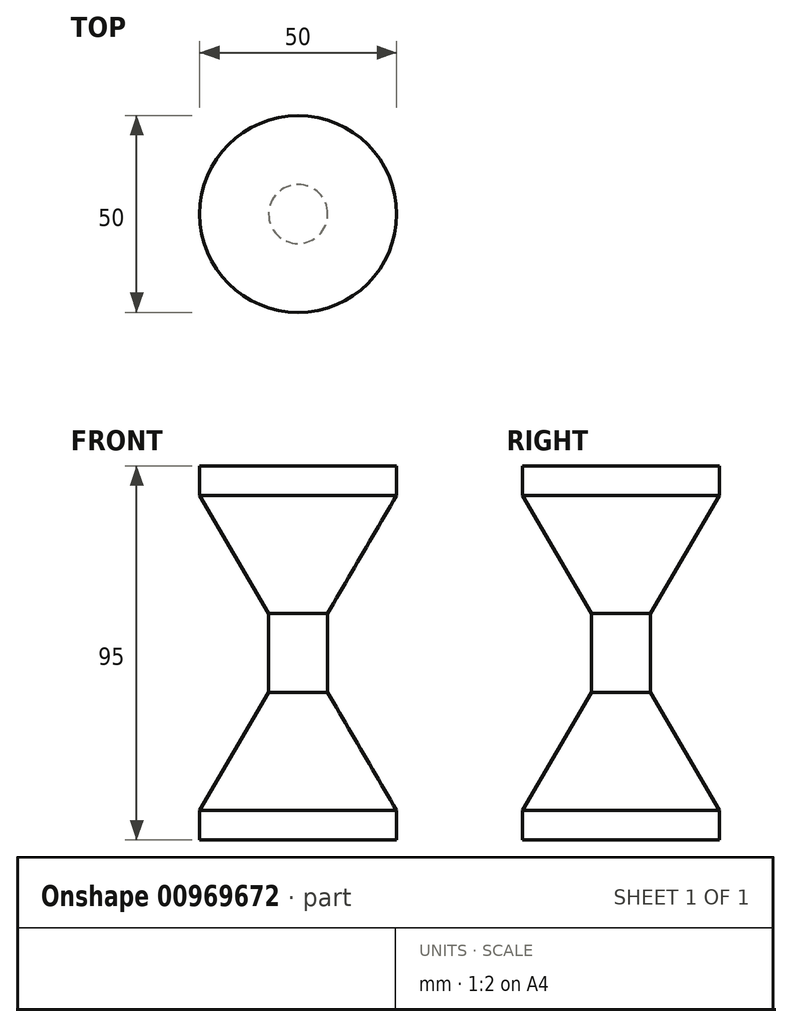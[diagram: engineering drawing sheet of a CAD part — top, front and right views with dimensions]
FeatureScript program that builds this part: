
annotation { "Feature Type Name" : "Feature", "Feature Type Description" : "" }
export const myFeature = defineFeature(function(context is Context, id is Id, definition is map)
    precondition{}
    {
        {
            var Q0;
            Q0=qCreatedBy(makeId("Right.planeOp"),FACE);
            var sketch = newSketch(context, id + "F0", { "sketchPlane" : qUnion([Q0])});
            skLineSegment(sketch, "E0", {"start": v(7.5, 10) * mm, "end": v(7.5, 0) * mm});
            skLineSegment(sketch, "E1", {"start": v(7.5, 10) * mm, "end": v(25, 40) * mm});
            skLineSegment(sketch, "E2", {"start": v(25, 40) * mm, "end": v(25, 47.5) * mm});
            skLineSegment(sketch, "E3.MirrorCS", {"start": v(7.5, -10) * mm, "end": v(7.5, 0) * mm});
            skLineSegment(sketch, "E4.MirrorCS", {"start": v(7.5, -10) * mm, "end": v(25, -40) * mm});
            skLineSegment(sketch, "E5.MirrorCS", {"start": v(25, -40) * mm, "end": v(25, -47.5) * mm});
            skLineSegment(sketch, "E6", {"start": v(0, 47.5) * mm, "end": v(0, -47.5) * mm, "construction": true});
            skLineSegment(sketch, "E7", {"start": v(25, 47.5) * mm, "end": v(0, 47.5) * mm});
            skLineSegment(sketch, "E8", {"start": v(0, -47.5) * mm, "end": v(25, -47.5) * mm});
            skLineSegment(sketch, "E9", {"start": v(0, -47.5) * mm, "end": v(0, 47.5) * mm});
            skSolve(sketch);
        }
        {
            var Q0;
            Q0 = qSketchRegion(id + "F0", true);
            var Q1;
            Q1=sQuery(id+"F0.wireOp",EDGE,"E6");
            revolve(context, id + "F1", {"surfaceOperationType" : NewSurfaceOperationType.NEW, "entities" : qUnion([Q0]), "axis" : qUnion([Q1]), "revolveType" : RevolveType.FULL});
        }
    });
